# Revit family: Legrand XL³ 125 cabinet
name_source: partatom
category: Equipement électrique
revit_build: Autodesk Revit 2018 (Build: 20170223_1515(x64)
units: mm (PartAtom-declared; Revit-internal decimal feet)

## family parameters
Basée sur le plan de construction = Oui
Configuration du panneau = Deux colonnes, circuits au sein
Cote de connecteur circulaire = Utiliser le diamètre
Couper avec des vides une fois chargée = Non
Numéro OmniClass = 23.80.30.11.17
Partagée = Non
Point de calcul de pièce = Non
Titre OmniClass = Distribution Boards and Control Panels
Toujours verticalement = Non
Type d'élément = Tableau de raccordement

## types (20) — shared parameters
Color = RAL 9003
Elévation par défaut = 1219 mm
Fabricant = legrand
General Conditions of Use = https://export.legrand.com
IK with door = 09
IK without door = 08
IP with door = 40
IP without door = 30
Material = Polystyrene
Modèle = XL³ 125
URL = www.legrand.com
width = 450 mm  [stored 1.47638 ft]

## per-type parameters (varying)
| type | 401611 | 401612 | 401613 | 401614 | 401631 | 401632 | 401633 | 401634 | 401641 | 401642 | 401643 | 401644 | 401646 | 401647 | 401648 | 401649 | 401656 | 401657 | 401658 | 401659 | Terminal block E | Terminal block N | depth | height |
| XL³ 125 cabinet 401611 | Oui | Non | Non | Non | Non | Non | Non | Non | Non | Non | Non | Non | Non | Non | Non | Non | Non | Non | Non | Non | automatic connection terminal block 5+18 holes Icc 10kA |  | 128 mm  [stored 0.419948 ft] | 300 mm |
| XL³ 125 cabinet 401612 | Non | Oui | Non | Non | Non | Non | Non | Non | Non | Non | Non | Non | Non | Non | Non | Non | Non | Non | Non | Non | automatic connection terminal block 5+27 holes Icc 10kA |  | 128 mm  [stored 0.419948 ft] | 450 mm  [stored 1.47638 ft] |
| XL³ 125 cabinet 401613 | Non | Non | Oui | Non | Non | Non | Non | Non | Non | Non | Non | Non | Non | Non | Non | Non | Non | Non | Non | Non | automatic connection terminal block 5+36 holes Icc 10kA |  | 125 mm  [stored 0.410105 ft] | 600 mm |
| XL³ 125 cabinet 401614 | Non | Non | Non | Oui | Non | Non | Non | Non | Non | Non | Non | Non | Non | Non | Non | Non | Non | Non | Non | Non | automatic connection terminal block 5+5+45 holes Icc 10kA |  | 128 mm  [stored 0.419948 ft] | 750 mm  [stored 2.46063 ft] |
| XL³ 125 cabinet 401631 | Non | Non | Non | Non | Oui | Non | Non | Non | Non | Non | Non | Non | Non | Non | Non | Non | Non | Non | Non | Non | automatic connection terminal block 5+18 holes Icc 10kA |  | 150 mm  [stored 0.492126 ft] | 300 mm |
| XL³ 125 cabinet 401641 | Non | Non | Non | Non | Non | Non | Non | Non | Oui | Non | Non | Non | Non | Non | Non | Non | Non | Non | Non | Non | automatic connection terminal block 5+18 holes Icc 10kA |  | 150 mm  [stored 0.492126 ft] | 300 mm |
| XL³ 125 cabinet 401646 | Non | Non | Non | Non | Non | Non | Non | Non | Non | Non | Non | Non | Oui | Non | Non | Non | Non | Non | Non | Non | terminal block 17 holes | terminal blocks 2x5 holes | 150 mm  [stored 0.492126 ft] | 300 mm |
| XL³ 125 cabinet 401656 | Non | Non | Non | Non | Non | Non | Non | Non | Non | Non | Non | Non | Non | Non | Non | Non | Oui | Non | Non | Non | terminal block 17 holes | terminal blocks 2x5 holes | 150 mm  [stored 0.492126 ft] | 300 mm |
| XL³ 125 cabinet 401632 | Non | Non | Non | Non | Non | Oui | Non | Non | Non | Non | Non | Non | Non | Non | Non | Non | Non | Non | Non | Non | automatic connection terminal block 5+27 holes Icc 10kA |  | 150 mm  [stored 0.492126 ft] | 450 mm  [stored 1.47638 ft] |
| XL³ 125 cabinet 401642 | Non | Non | Non | Non | Non | Non | Non | Non | Non | Oui | Non | Non | Non | Non | Non | Non | Non | Non | Non | Non | automatic connection terminal block 5+27 holes Icc 10kA |  | 150 mm  [stored 0.492126 ft] | 450 mm  [stored 1.47638 ft] |
| XL³ 125 cabinet 401647 | Non | Non | Non | Non | Non | Non | Non | Non | Non | Non | Non | Non | Non | Oui | Non | Non | Non | Non | Non | Non | terminal block 22 holes | terminal blocks 3x8 holes | 150 mm  [stored 0.492126 ft] | 450 mm  [stored 1.47638 ft] |
| XL³ 125 cabinet 401657 | Non | Non | Non | Non | Non | Non | Non | Non | Non | Non | Non | Non | Non | Non | Non | Non | Non | Oui | Non | Non | terminal block 22 holes | terminal blocks 3x8 holes | 150 mm  [stored 0.492126 ft] | 450 mm  [stored 1.47638 ft] |
| XL³ 125 cabinet 401633 | Non | Non | Non | Non | Non | Non | Oui | Non | Non | Non | Non | Non | Non | Non | Non | Non | Non | Non | Non | Non | automatic connection terminal block 5+36 holes Icc 10kA |  | 150 mm  [stored 0.492126 ft] | 600 mm |
| XL³ 125 cabinet 401643 | Non | Non | Non | Non | Non | Non | Non | Non | Non | Non | Oui | Non | Non | Non | Non | Non | Non | Non | Non | Non | automatic connection terminal block 5+36 holes Icc 10kA |  | 150 mm  [stored 0.492126 ft] | 600 mm |
| XL³ 125 cabinet 401648 | Non | Non | Non | Non | Non | Non | Non | Non | Non | Non | Non | Non | Non | Non | Oui | Non | Non | Non | Non | Non | terminal blocks 27 holes | terminal blocks 4x8 holes | 150 mm  [stored 0.492126 ft] | 600 mm |
| XL³ 125 cabinet 401658 | Non | Non | Non | Non | Non | Non | Non | Non | Non | Non | Non | Non | Non | Non | Non | Non | Non | Non | Oui | Non | terminal blocks 27 holes | terminal blocks 4x8 holes | 150 mm  [stored 0.492126 ft] | 600 mm |
| XL³ 125 cabinet 401634 | Non | Non | Non | Non | Non | Non | Non | Oui | Non | Non | Non | Non | Non | Non | Non | Non | Non | Non | Non | Non | automatic connection terminal block 5+5+45 holes Icc 10kA |  | 150 mm  [stored 0.492126 ft] | 750 mm  [stored 2.46063 ft] |
| XL³ 125 cabinet 401644 | Non | Non | Non | Non | Non | Non | Non | Non | Non | Non | Non | Oui | Non | Non | Non | Non | Non | Non | Non | Non | automatic connection terminal block 5+5+45 holes Icc 10kA |  | 150 mm  [stored 0.492126 ft] | 750 mm  [stored 2.46063 ft] |
| XL³ 125 cabinet 401649 | Non | Non | Non | Non | Non | Non | Non | Non | Non | Non | Non | Non | Non | Non | Non | Oui | Non | Non | Non | Non | terminal block 35 holes | terminal blocks 5x8 holes | 150 mm  [stored 0.492126 ft] | 750 mm  [stored 2.46063 ft] |
| XL³ 125 cabinet 401659 | Non | Non | Non | Non | Non | Non | Non | Non | Non | Non | Non | Non | Non | Non | Non | Non | Non | Non | Non | Oui | terminal block 35 holes | terminal blocks 5x8 holes | 150 mm  [stored 0.492126 ft] | 750 mm  [stored 2.46063 ft] |

note: [stored X ft] marks values corroborated as IEEE doubles in the binary element streams (Revit-internal decimal feet)
